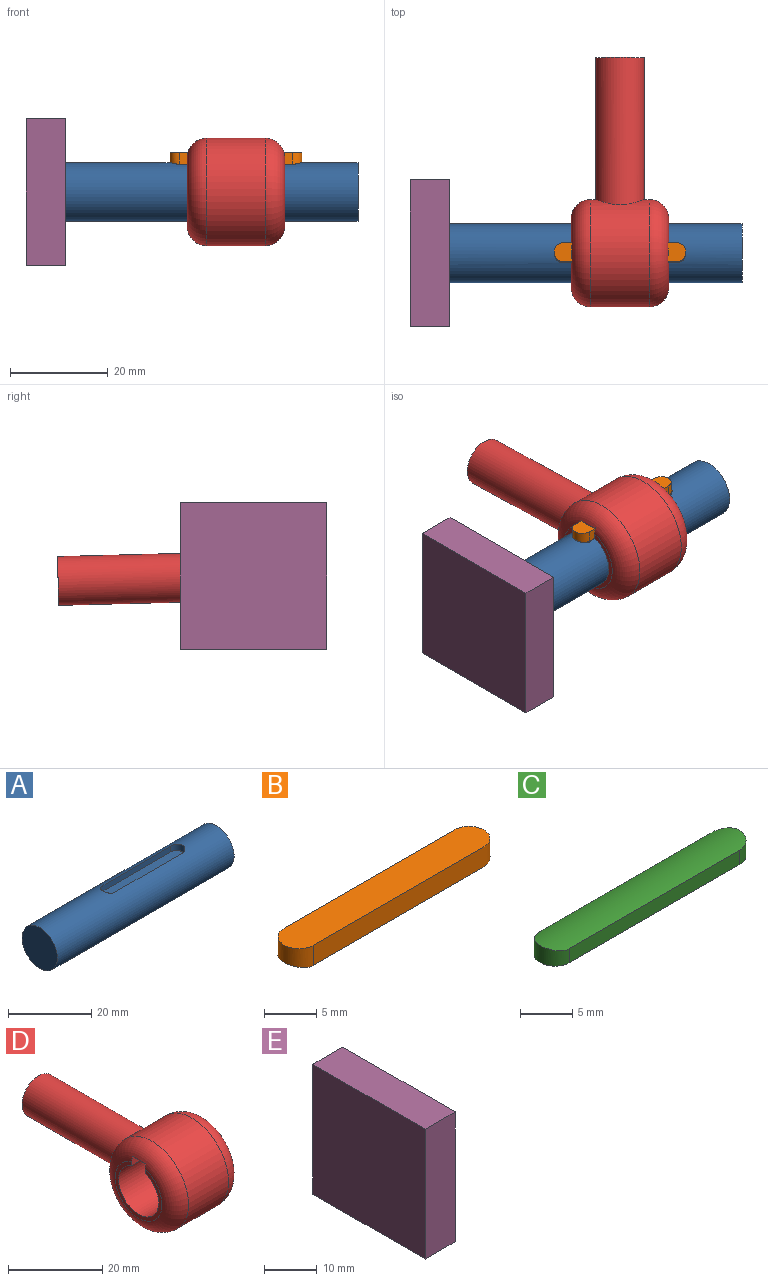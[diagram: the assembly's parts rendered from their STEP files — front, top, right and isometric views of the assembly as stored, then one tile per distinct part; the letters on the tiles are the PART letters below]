
ASSEMBLY  parts=5 mates=4
PART A: 8 faces, bbox 60x12x12 mm
  f0: cylinder r=6mm len=60mm, axis (1,0,0), area 2155.4mm2, adj f1,f2,f3,f4,f5,f6
  f1: plane 12x12mm, normal (-1,0,0), area 113.1mm2, adj f0
  f2: plane 12x12mm, normal (1,0,0), area 113.1mm2, adj f0
  f3: plane 23x1.66mm, normal (0,1,0), area 38.1mm2, adj f0,f4,f6,f7
  f4: cylinder r=2mm len=4mm, axis (0,0,-1), area 11.5mm2, adj f0,f3,f5,f7
  f5: plane 23x1.66mm, normal (0,-1,0), area 38.1mm2, adj f0,f4,f6,f7
  f6: cylinder r=2mm len=4mm, axis (0,0,-1), area 11.5mm2, adj f0,f3,f5,f7
  f7: plane 27x4mm, normal (0,0,1), area 104.6mm2, adj f3,f4,f5,f6
PART B: 6 faces, bbox 27x4x2.3 mm
  f0: plane 23x2.34mm, normal (0,-1,0), area 53.9mm2, adj f1,f3,f4,f5
  f1: cylinder r=2mm len=4mm, axis (0,0,-1), area 13.6mm2, adj f0,f2,f4,f5
  f2: plane 23x2.34mm, normal (0,1,0), area 53.9mm2, adj f1,f3,f4,f5
  f3: cylinder r=2mm len=4mm, axis (0,0,-1), area 13.6mm2, adj f0,f2,f4,f5
  f4: plane 27x4mm, normal (0,0,1), area 104.6mm2, adj f0,f1,f2,f3
  f5: cylinder r=6mm len=27mm, axis (-1,0,0), area 106.5mm2, adj f0,f1,f2,f3
PART C: 6 faces, bbox 27x4x2 mm
  f0: plane 27x4mm, normal (0,0,-1), area 104.6mm2, adj f1,f2,f3,f4
  f1: cylinder r=2mm len=4mm, axis (0,0,-1), area 11.5mm2, adj f0,f2,f4,f5
  f2: plane 23x1.66mm, normal (0,1,0), area 38.1mm2, adj f0,f1,f3,f5
  f3: cylinder r=2mm len=4mm, axis (0,0,-1), area 11.5mm2, adj f0,f2,f4,f5
  f4: plane 23x1.66mm, normal (0,-1,0), area 38.1mm2, adj f0,f1,f3,f5
  f5: cylinder r=6mm len=27mm, axis (-1,0,0), area 106.5mm2, adj f1,f2,f3,f4
PART D: 11 faces, bbox 20x51.9x23.8 mm
  f0: cylinder r=6mm len=20mm, axis (-1,0,0), area 672.4mm2, adj f1,f3,f5,f6
  f1: plane 20.03x2.38mm, normal (0,1,0), area 46.7mm2, adj f0,f2,f5,f6,f7,f8
  f2: plane 19.75x4mm, normal (0,0,-1), area 78.8mm2, adj f1,f3,f7,f8
  f3: plane 20.03x2.38mm, normal (0,-1,0), area 46.7mm2, adj f0,f2,f5,f6,f7,f8
  f4: cylinder r=11mm len=22mm, axis (-1,0,0), area 748.9mm2, adj f7,f8,f10
  f5: plane 14x13.71mm, normal (1,0,0), area 36.8mm2, adj f0,f1,f3,f8
  f6: plane 14x13.71mm, normal (-1,0,0), area 36.8mm2, adj f0,f1,f3,f7
  f7: torus R=7mm, axis (1,0,0), area 372.4mm2, adj f1,f2,f3,f4,f6
  f8: torus R=7mm, axis (1,0,0), area 372.4mm2, adj f1,f2,f3,f4,f5
  f9: plane 10x10mm, normal (0,1,0), area 78.5mm2, adj f10
  f10: cylinder r=5mm len=30.2mm, axis (0,1,0), area 929.6mm2, adj f4,f9
PART E: 6 faces, bbox 8x30x30 mm
  f0: plane 30x8mm, normal (0,0,-1), area 240mm2, adj f1,f3,f4,f5
  f1: plane 30x8mm, normal (0,-1,0), area 240mm2, adj f0,f2,f4,f5
  f2: plane 30x8mm, normal (0,0,1), area 240mm2, adj f1,f3,f4,f5
  f3: plane 30x8mm, normal (0,1,0), area 240mm2, adj f0,f2,f4,f5
  f4: plane 30x30mm, normal (-1,0,0), area 900mm2, adj f0,f1,f2,f3
  f5: plane 30x30mm, normal (1,0,0), area 900mm2, adj f0,f1,f2,f3
PLACE A t=(-10.89,-24.64,20.67)mm
PLACE B rot(axis=(-1,0,0),1.5deg) t=(-10.89,-24.64,20.66)mm
PLACE C t=(-10.89,-24.64,20.67)mm
PLACE D rot(axis=(-1,0,0),1.5deg) t=(-10.89,-24.64,20.67)mm
PLACE E t=(-10.89,-24.64,20.67)mm fixed
MATE fastened C.f2 <-> A.f5  axis (0,1,0) through (-35.89,-22.64,25.5)mm
MATE fastened D.f3 <-> B.f2  axis (0,-1,0.03) through (-35.89,-22.47,27.44)mm
MATE fastened A.f0 <-> E.f5  axis (-1,0,0) through (-70.89,-24.64,20.67)mm
MATE revolute D.f0 <-> A.f0  axis (-1,0,0) through (-35.89,-24.64,20.67)mm
